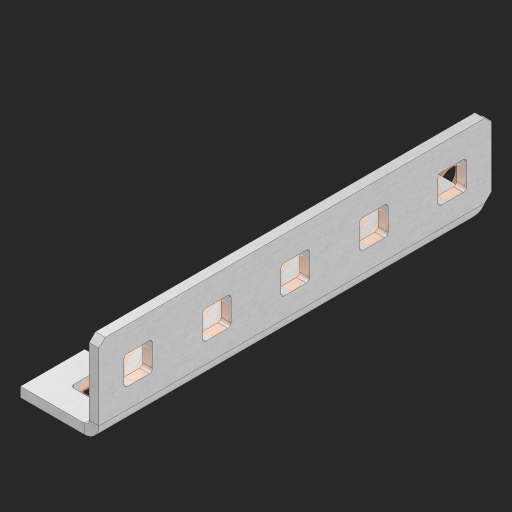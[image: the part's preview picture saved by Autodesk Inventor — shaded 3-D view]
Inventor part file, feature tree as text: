
AUTODESK INVENTOR PART (.ipt)
format: ipt  version: 2023 (Build 270158000, 158)  size: 602,112 bytes
history: native  units: in
note: dims shown in document units (in); Inventor stores cm internally (conversion verified against a paired STEP export)
features: other x163, extrude x13, sheet_metal_op x11, sketch x10, pattern_linear x2, mirror x1, chamfer x1
ambient origin geometry x8: Origin, YZ Plane, XZ Plane, XY Plane, X Axis, Y Axis, Z Axis, Center Point
bodies: Solid1 (feature_tree), Body (feature_tree)
feature tree (201):
  other  "Alu Half C 1x2x1x5"
  other  "Table"
  other  "Alu C 1x2x1x35"
  other  "Alu C 1x2x1x34"
  other  "Alu C 1x2x1x33"
  other  "Alu C 1x2x1x32"
  other  "Alu C 1x2x1x31"
  other  "Alu C 1x2x1x30"
  other  "Alu C 1x2x1x29"
  other  "Alu C 1x2x1x28"
  other  "Alu C 1x2x1x27"
  other  "Alu C 1x2x1x26"
  other  "Alu C 1x2x1x25"
  other  "Alu C 1x2x1x24"
  other  "Alu C 1x2x1x23"
  other  "Alu C 1x2x1x22"
  other  "Alu C 1x2x1x21"
  other  "Alu C 1x2x1x20"
  other  "Alu C 1x2x1x19"
  other  "Alu C 1x2x1x18"
  other  "Alu C 1x2x1x17"
  other  "Alu C 1x2x1x16"
  other  "Alu C 1x2x1x15"
  other  "Alu C 1x2x1x14"
  other  "Alu C 1x2x1x13"
  other  "Alu C 1x2x1x12"
  other  "Alu C 1x2x1x11"
  other  "Alu C 1x2x1x10"
  other  "Alu C 1x2x1x9"
  other  "Alu C 1x2x1x8"
  other  "Alu C 1x2x1x7"
  other  "Alu C 1x2x1x6"
  other  "Alu C 1x2x1x5"
  other  "Alu C 1x2x1x4"
  other  "Alu C 1x2x1x3"
  other  "Alu C 1x2x1x2"
  other  "Alu C 1x2x1x1"
  other  "Steel C 1x2x1x35"
  other  "Steel C 1x2x1x34"
  other  "Steel C 1x2x1x33"
  other  "Steel C 1x2x1x32"
  other  "Steel C 1x2x1x31"
  other  "Steel C 1x2x1x30"
  other  "Steel C 1x2x1x29"
  other  "Steel C 1x2x1x28"
  other  "Steel C 1x2x1x27"
  other  "Steel C 1x2x1x26"
  other  "Steel C 1x2x1x25"
  other  "Steel C 1x2x1x24"
  other  "Steel C 1x2x1x23"
  other  "Steel C 1x2x1x22"
  other  "Steel C 1x2x1x21"
  other  "Steel C 1x2x1x20"
  other  "Steel C 1x2x1x19"
  other  "Steel C 1x2x1x18"
  other  "Steel C 1x2x1x17"
  other  "Steel C 1x2x1x16"
  other  "Steel C 1x2x1x15"
  other  "Steel C 1x2x1x14"
  other  "Steel C 1x2x1x13"
  other  "Steel C 1x2x1x12"
  other  "Steel C 1x2x1x11"
  other  "Steel C 1x2x1x10"
  other  "Steel C 1x2x1x9"
  other  "Steel C 1x2x1x8"
  other  "Steel C 1x2x1x7"
  other  "Steel C 1x2x1x6"
  other  "Steel C 1x2x1x5"
  other  "Steel C 1x2x1x4"
  other  "Steel C 1x2x1x3"
  other  "Steel C 1x2x1x2"
  other  "Steel C 1x2x1x1"
  other  "Alu Half C 1x2x1x35"
  other  "Alu Half C 1x2x1x34"
  other  "Alu Half C 1x2x1x33"
  other  "Alu Half C 1x2x1x32"
  other  "Alu Half C 1x2x1x31"
  other  "Alu Half C 1x2x1x30"
  other  "Alu Half C 1x2x1x29"
  other  "Alu Half C 1x2x1x28"
  other  "Alu Half C 1x2x1x27"
  other  "Alu Half C 1x2x1x26"
  other  "Alu Half C 1x2x1x25"
  other  "Alu Half C 1x2x1x24"
  other  "Alu Half C 1x2x1x23"
  other  "Alu Half C 1x2x1x22"
  other  "Alu Half C 1x2x1x21"
  other  "Alu Half C 1x2x1x20"
  other  "Alu Half C 1x2x1x19"
  other  "Alu Half C 1x2x1x18"
  other  "Alu Half C 1x2x1x17"
  other  "Alu Half C 1x2x1x16"
  other  "Alu Half C 1x2x1x15"
  other  "Alu Half C 1x2x1x14"
  other  "Alu Half C 1x2x1x13"
  other  "Alu Half C 1x2x1x12"
  other  "Alu Half C 1x2x1x11"
  other  "Alu Half C 1x2x1x10"
  other  "Alu Half C 1x2x1x9"
  other  "Alu Half C 1x2x1x8"
  other  "Alu Half C 1x2x1x7"
  other  "Alu Half C 1x2x1x6"
  other  "Alu Half C 1x2x1x4"
  other  "Alu Half C 1x2x1x3"
  other  "Alu Half C 1x2x1x2"
  other  "Alu Half C 1x2x1x1"
  other  "Steel Half C 1x2x1x35"
  other  "Steel Half C 1x2x1x34"
  other  "Steel Half C 1x2x1x33"
  other  "Steel Half C 1x2x1x32"
  other  "Steel Half C 1x2x1x31"
  other  "Steel Half C 1x2x1x30"
  other  "Steel Half C 1x2x1x29"
  other  "Steel Half C 1x2x1x28"
  other  "Steel Half C 1x2x1x27"
  other  "Steel Half C 1x2x1x26"
  other  "Steel Half C 1x2x1x25"
  other  "Steel Half C 1x2x1x24"
  other  "Steel Half C 1x2x1x23"
  other  "Steel Half C 1x2x1x22"
  other  "Steel Half C 1x2x1x21"
  other  "Steel Half C 1x2x1x20"
  other  "Steel Half C 1x2x1x19"
  other  "Steel Half C 1x2x1x18"
  other  "Steel Half C 1x2x1x17"
  other  "Steel Half C 1x2x1x16"
  other  "Steel Half C 1x2x1x15"
  other  "Steel Half C 1x2x1x14"
  other  "Steel Half C 1x2x1x13"
  other  "Steel Half C 1x2x1x12"
  other  "Steel Half C 1x2x1x11"
  other  "Steel Half C 1x2x1x10"
  other  "Steel Half C 1x2x1x9"
  other  "Steel Half C 1x2x1x8"
  other  "Steel Half C 1x2x1x7"
  other  "Steel Half C 1x2x1x6"
  other  "Steel Half C 1x2x1x5"
  other  "Steel Half C 1x2x1x4"
  other  "Steel Half C 1x2x1x3"
  other  "Steel Half C 1x2x1x2"
  other  "Steel Half C 1x2x1x1"
  sheet_metal_op  "Flanges"
  other  "Flange Pattern Plane"
  other  "Flange Pattern Sketch"
  sheet_metal_op  "Flange Pattern"
  sheet_metal_op  "Body Pattern"
  pattern_linear  "Center Pattern"  Spacing1=0.0625in  [1 undecoded]
  other  "Arc Length"
  mirror  "Notch Mirror"
  pattern_linear  "Notch Pattern"  Spacing1=0.182in  [1 undecoded]
  chamfer  "End Chamfer"
  extrude  "Half Cut"  Depth=0.02in
  sketch  "Sketch1"  dims[d0=1.0in]
  other  "Plate1"
  sketch  "Sketch2"  dims[d1=2.5in]
  other  "Plate2"
  sheet_metal_op  "Bend1"
  sheet_metal_op  "Corner1"
  sketch  "Sketch3"  dims[d2=0.0625in]
  sketch  "Sketch7"  dims[d3=0.0625in]
  other  "Srf1"
  other  "Srf2"
  sketch  "Sketch8"  dims[d4=0.0312in]
  sketch  "Sketch9"  dims[d5=0.125in]
  other  "Srf91"
  sheet_metal_op  "Body Pattern Sketch"
  other  "Srf92"
  sketch  "Sketch13"  dims[d6=0.0625in]
  sketch  "Sketch14"  dims[d7=0.5in d8=90.0deg d9=0.0312in]
  sketch  "Sketch15"  dims[d10=0.25in]
  sketch  "Sketch16"  dims[d11=0.0625in d12=0.0625in d16=0.182in d17=0.02in d18=0.0625in d19=0.0in d20=0.25in d21=0.25in d38=1.9685in d40=0.5in d41=0.3937in d43=1.0in d46=0.172in d47=1.0in d48=0.0in d49=0.182in d50=0.02in d51=0.25in d52=0.25in d53=0.0625in d54=0.0in d55=0.172in d56=1.0in d57=0.0in d58=0.25in d60=1.9685in d62=0.5in d63=0.3937in d65=0.5in d85=0.1473in d86=0.1782in d88=0.04in d89=0.0625in d90=0.0in d91=0.04in d92=0.0491in d95=2.5in d96=0.04in d97=0.25in d98=45.0deg d99=0.25in d100=0.5in d101=0.0in d102=2.497in d106=0.182in d107=0.02in d108=0.5in d109=0.5in d110=0.0625in d111=0.0in d112=0.172in d113=0.5in d114=0.0in d117=0.5in d118=0.5in d119=0.5in]
  other  "Srf786"
  other  "Srf823"
  other  "Srf824"
  other  "Srf825"
  other  "Srf856"
  other  "Srf857"
  other  "Srf858"
  other  "Srf889"
  other  "Srf890"
  other  "Srf891"
  other  "Srf892"
  sheet_metal_op  "Flange Stamp"
  sheet_metal_op  "Flange Circle"
  sheet_metal_op  "Body Stamp"
  sheet_metal_op  "Body Circle"
  other  "Center Stamp"
  other  "Center Circle"
  sheet_metal_op  "Notch"
  extrude  "ExtrusionSrf2"  Depth=0.0625in
  extrude  "ExtrusionSrf92"  TaperAngle=0.0deg  [1 undecoded]
  extrude  "ExtrusionSrf823"  Depth=0.5in
  extrude  "ExtrusionSrf824"  Depth=0.5in
  extrude  "ExtrusionSrf825"  Depth=0.5in
  extrude  "ExtrusionSrf856"  Depth=0.5in
  extrude  "ExtrusionSrf857"  Depth=1.0in TaperAngle=0.0deg
  extrude  "ExtrusionSrf858"  Depth=0.182in
  extrude  "ExtrusionSrf889"  Depth=0.02in
  extrude  "ExtrusionSrf890"  Depth=0.5in
  extrude  "ExtrusionSrf891"  Depth=0.5in
  extrude  "ExtrusionSrf892"  Depth=0.0625in
note: 3 required parameter values undecoded (feature->parameter linkage not recoverable at this tier; creation-order binding heuristic only, values carry confidence <= 0.55)
